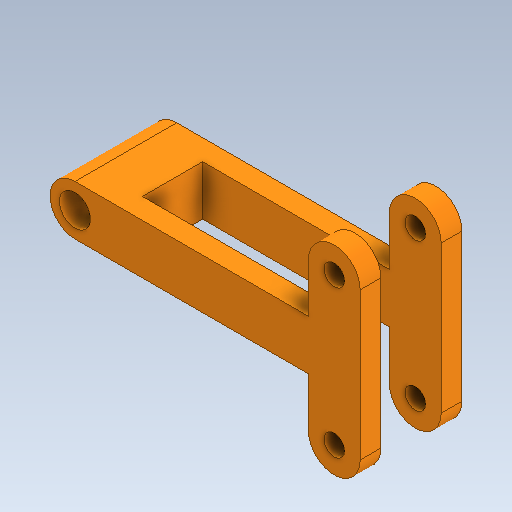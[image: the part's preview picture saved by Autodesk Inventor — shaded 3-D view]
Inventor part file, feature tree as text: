
AUTODESK INVENTOR PART (.ipt)
format: ipt  version: 2020 (Build 240168000, 168)  size: 153,088 bytes
history: native  units: in
note: dims shown in document units (in); Inventor stores cm internally (conversion verified against a paired STEP export)
features: other x3, sketch x3
ambient origin geometry x8: Origin, YZ Plane, XZ Plane, XY Plane, X Axis, Y Axis, Z Axis, Center Point
bodies: Solid1 (feature_tree)
feature tree (6):
  other  "PistonCasingPivot.ipt"
  other  "Solid1::PistonCasingPivot.ipt"
  other  "TaggingFeature1"
  sketch  "Sketch1"  dims[d0=0.3937in]
  sketch  "Sketch2"
  sketch  "Sketch4"
